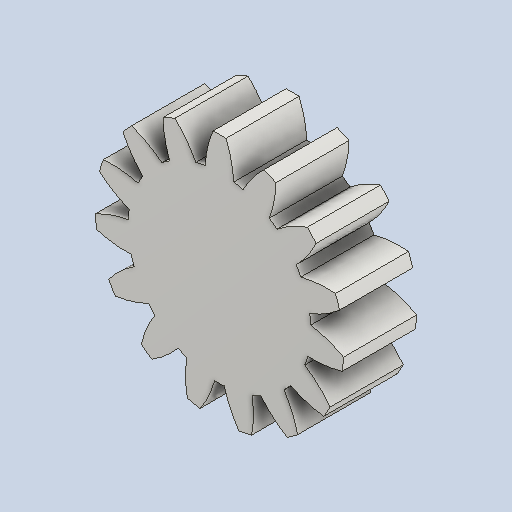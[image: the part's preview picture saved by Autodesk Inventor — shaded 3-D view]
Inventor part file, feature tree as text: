
AUTODESK INVENTOR PART (.ipt)
format: ipt  version: 2024 (Build 280153000, 153)  size: 224,256 bytes
history: native  units: mm (DEFAULTED — no unit token found)
features: plane x3, other x3, extrude x1, sketch x1
ambient origin geometry x8: Origin, YZ Plane, XZ Plane, XY Plane, X Axis, Y Axis, Z Axis, Center Point
bodies: Solid1 (feature_tree)
feature tree (8):
  extrude  "Extrusion1"  Depth=10.0mm TaperAngle=0.0deg
  plane  "Work Plane2"
  plane  "Work Plane8"
  plane  "Work Plane9"
  other  "Spur Gear"
  sketch  "Sketch1"  dims[d0=34.0mm d1=10.0mm d2=0.0mm d3=30.0mm d4=10.0mm d5=0.0mm d16=25.0mm d17=0.0mm d34=2.094395mm d39=0.0mm d41=0.0mm d43=25.0mm d46=25.0mm d47=0.0mm d48=0.0mm]
  other  "Srf1"
  other  "Pitch Diameter"
